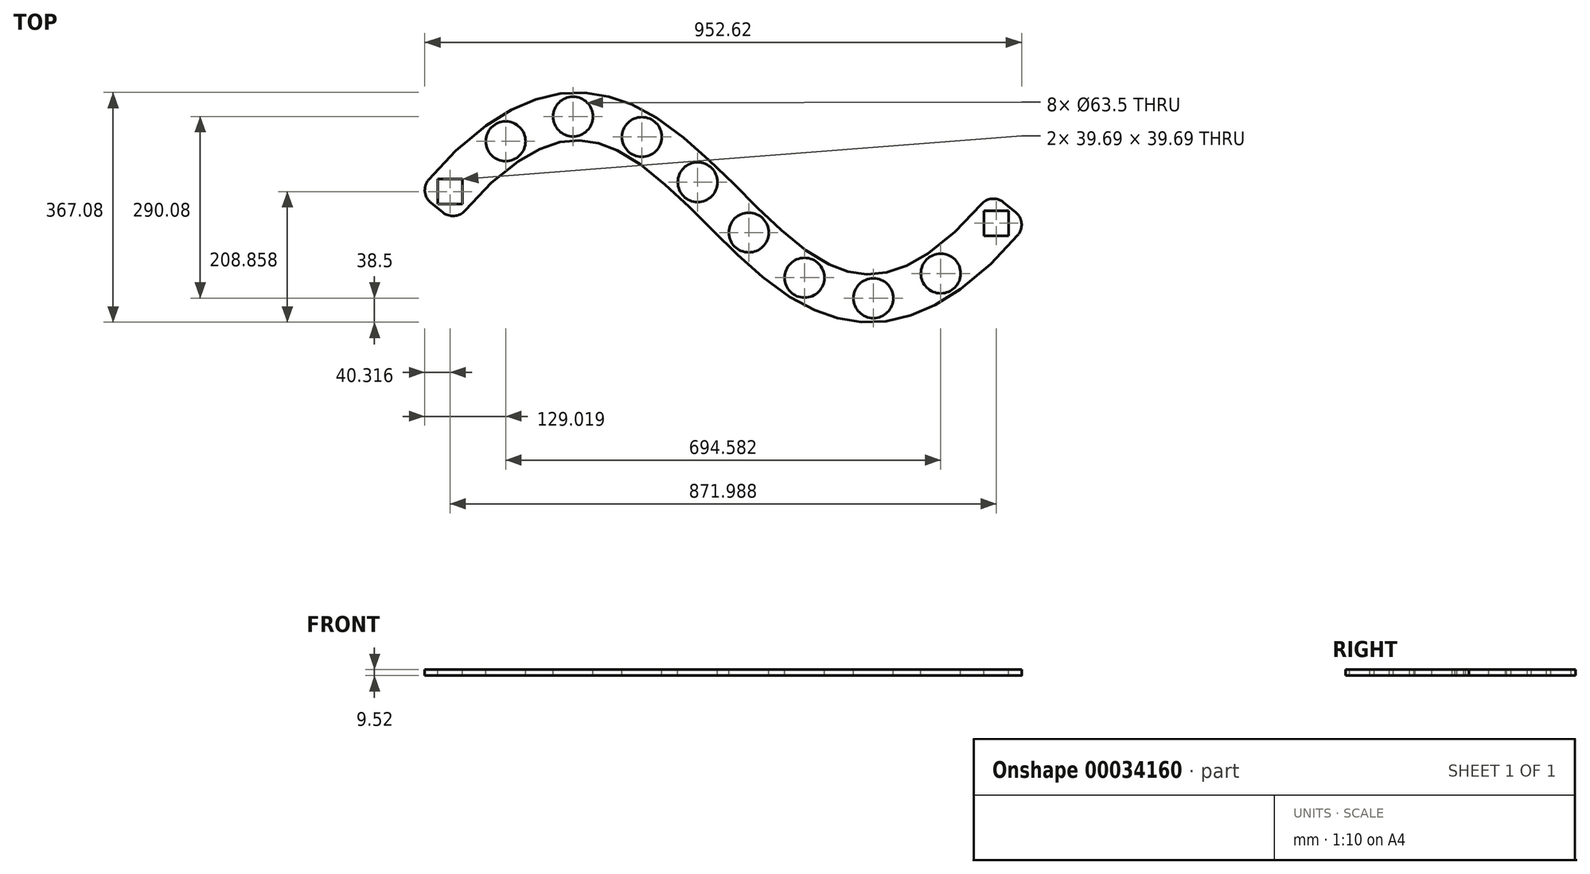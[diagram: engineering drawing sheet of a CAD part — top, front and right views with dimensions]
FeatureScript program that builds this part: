
annotation { "Feature Type Name" : "Feature", "Feature Type Description" : "" }
export const myFeature = defineFeature(function(context is Context, id is Id, definition is map)
    precondition{}
    {
        {
            var Q0;
            Q0=qCreatedBy(makeId("Top.planeOp"),FACE);
            var sketch = newSketch(context, id + "F0", { "sketchPlane" : qUnion([Q0])});
            skFitSpline(sketch, "E0", {"points": [v(457.2, 0) * mm, v(0, 0) * mm, v(-457.2, 0) * mm], "startDerivative": vector(-1234.52, -1508.68) * mm, "endDerivative": vector(-1234.52, -1508.68) * mm, "construction": true});
            skLineSegment(sketch, "E1", {"start": v(-251.45, 251.45) * mm, "end": v(251.45, -251.45) * mm, "construction": true});
            skFitSpline(sketch, "E2.0", {"points": [v(427.71, 24.13) * mm, v(415.4, 9.08) * mm, v(391.56, -17.97) * mm, v(358.18, -49.96) * mm, v(332.45, -69.99) * mm, v(313.15, -82.4) * mm, v(299.33, -90.03) * mm, v(286.14, -96.08) * mm, v(273.56, -100.69) * mm, v(261.55, -103.98) * mm, v(250.01, -106.09) * mm, v(238.86, -107.1) * mm, v(227.98, -107.12) * mm, v(217.27, -106.2) * mm, v(206.62, -104.35) * mm, v(195.97, -101.6) * mm, v(185.25, -97.95) * mm, v(174.44, -93.43) * mm, v(159.9, -86.24) * mm, v(141.47, -75.14) * mm, v(119.04, -58.8) * mm, v(96.37, -39.9) * mm, v(73.49, -18.95) * mm, v(50.39, 3.5) * mm, v(27, 26.88) * mm, v(3.24, 50.64) * mm, v(-21.04, 74.24) * mm, v(-46, 97.12) * mm, v(-71.89, 118.73) * mm, v(-98.95, 138.49) * mm, v(-122.74, 152.87) * mm, v(-142.68, 162.75) * mm, v(-158.11, 169.22) * mm, v(-174.04, 174.65) * mm, v(-190.48, 178.9) * mm, v(-207.39, 181.84) * mm, v(-224.73, 183.35) * mm, v(-242.44, 183.32) * mm, v(-260.43, 181.67) * mm, v(-278.62, 178.34) * mm, v(-296.95, 173.3) * mm, v(-315.36, 166.54) * mm, v(-333.84, 158.04) * mm, v(-352.38, 147.8) * mm, v(-377.21, 131.8) * mm, v(-408.54, 107.32) * mm, v(-446.94, 70.43) * mm, v(-473.28, 40.51) * mm, v(-486.69, 24.13) * mm]});
            skLineSegment(sketch, "E3", {"start": v(-486.69, 24.13) * mm, "end": v(-457.2, 0) * mm});
            skLineSegment(sketch, "E4", {"start": v(427.71, 24.13) * mm, "end": v(457.2, 0) * mm});
            skFitSpline(sketch, "E5.0", {"points": [v(486.69, -24.13) * mm, v(473.28, -40.51) * mm, v(446.94, -70.43) * mm, v(408.54, -107.32) * mm, v(377.21, -131.8) * mm, v(352.38, -147.8) * mm, v(333.84, -158.04) * mm, v(315.36, -166.54) * mm, v(296.95, -173.3) * mm, v(278.62, -178.34) * mm, v(260.43, -181.67) * mm, v(242.44, -183.32) * mm, v(224.73, -183.35) * mm, v(207.39, -181.84) * mm, v(190.48, -178.9) * mm, v(174.04, -174.65) * mm, v(158.11, -169.22) * mm, v(142.68, -162.75) * mm, v(122.74, -152.87) * mm, v(98.95, -138.49) * mm, v(71.89, -118.73) * mm, v(46, -97.12) * mm, v(21.04, -74.24) * mm, v(-3.24, -50.64) * mm, v(-27, -26.88) * mm, v(-50.39, -3.5) * mm, v(-73.49, 18.95) * mm, v(-96.37, 39.9) * mm, v(-119.04, 58.8) * mm, v(-141.47, 75.14) * mm, v(-159.9, 86.24) * mm, v(-174.44, 93.43) * mm, v(-185.25, 97.95) * mm, v(-195.97, 101.6) * mm, v(-206.62, 104.35) * mm, v(-217.27, 106.2) * mm, v(-227.98, 107.12) * mm, v(-238.86, 107.1) * mm, v(-250.01, 106.09) * mm, v(-261.55, 103.98) * mm, v(-273.56, 100.69) * mm, v(-286.14, 96.08) * mm, v(-299.33, 90.03) * mm, v(-313.15, 82.4) * mm, v(-332.45, 69.99) * mm, v(-358.18, 49.96) * mm, v(-391.56, 17.97) * mm, v(-415.4, -9.08) * mm, v(-427.71, -24.13) * mm]});
            skLineSegment(sketch, "E6", {"start": v(-457.2, 0) * mm, "end": v(-427.71, -24.13) * mm});
            skLineSegment(sketch, "E7", {"start": v(457.2, 0) * mm, "end": v(486.69, -24.13) * mm});
            skLineSegment(sketch, "E8", {"start": v(457.2, 0) * mm, "end": v(-457.2, 0) * mm, "construction": true});
            skSolve(sketch);
        }
        {
            var Q0;
            Q0=makeQuery(id+"F0.imprint","IMPRINT",FACE,{"disambiguationData":[TD([[makeQuery(id+"F0.imprint","IMPRINT",EDGE,{"derivedFrom":sQuery(id+"F0.wireOp",EDGE,"E0")}),-1.0]])]});
            var Q1;
            Q1=makeQuery(id+"F0.imprint","IMPRINT",FACE,{"disambiguationData":[TD([[makeQuery(id+"F0.imprint","IMPRINT",EDGE,{"derivedFrom":sQuery(id+"F0.wireOp",EDGE,"E2.0")}),1.0]])]});
            extrude(context, id + "F1", {"entities" : qUnion([Q0, Q1]), "endBound" : BoundingType.SYMMETRIC, "depth" : 9.52 * mm});
        }
        {
            var Q0;
            Q0=makeQuery(id+"F1.opExtrude","SWEPT_EDGE",EDGE,{"disambiguationData":[OSD([sQuery(id+"F0.wireOp",EDGE,"E5.0"),sQuery(id+"F0.wireOp",EDGE,"E6")])]});
            var Q1;
            Q1=makeQuery(id+"F1.opExtrude","SWEPT_EDGE",EDGE,{"disambiguationData":[OSD([sQuery(id+"F0.wireOp",EDGE,"E2.0"),sQuery(id+"F0.wireOp",EDGE,"E3")])]});
            var Q2;
            Q2=makeQuery(id+"F1.opExtrude","SWEPT_EDGE",EDGE,{"disambiguationData":[OSD([sQuery(id+"F0.wireOp",EDGE,"E5.0"),sQuery(id+"F0.wireOp",EDGE,"E7")])]});
            var Q3;
            Q3=makeQuery(id+"F1.opExtrude","SWEPT_EDGE",EDGE,{"disambiguationData":[OSD([sQuery(id+"F0.wireOp",EDGE,"E2.0"),sQuery(id+"F0.wireOp",EDGE,"E4")])]});
            fillet(context, id + "F2", {"entities" : qUnion([Q0, Q1, Q2, Q3]), "radius" : 25.4 * mm, "tangentPropagation" : true, "allowEdgeOverflow" : false});
        }
        {
            var Q0;
            Q0=makeQuery(id+"F1.opExtrude","CAP_FACE",FACE,{"disambiguationData":[OSD([sQuery(id+"F0.wireOp",EDGE,"E2.0"),sQuery(id+"F0.wireOp",EDGE,"E3"),sQuery(id+"F0.wireOp",EDGE,"E4"),sQuery(id+"F0.wireOp",EDGE,"E5.0"),sQuery(id+"F0.wireOp",EDGE,"E6"),sQuery(id+"F0.wireOp",EDGE,"E7")])],"isStart":false});
            var sketch = newSketch(context, id + "F3", { "sketchPlane" : qUnion([Q0])});
            skLineSegment(sketch, "E9.rect.bottom", {"start": v(-416.15, 45.16) * mm, "end": v(-455.84, 45.16) * mm});
            skLineSegment(sketch, "E9.rect.top", {"start": v(-416.15, 5.47) * mm, "end": v(-455.84, 5.47) * mm});
            skLineSegment(sketch, "E9.rect.left", {"start": v(-416.15, 45.16) * mm, "end": v(-416.15, 5.47) * mm});
            skLineSegment(sketch, "E9.rect.right", {"start": v(-455.84, 45.16) * mm, "end": v(-455.84, 5.47) * mm});
            skPoint(sketch, "E9.rect.middle", {"position": v(-436, 25.32) * mm});
            skLineSegment(sketch, "E10.rect.bottom", {"start": v(455.84, -5.47) * mm, "end": v(416.15, -5.47) * mm});
            skLineSegment(sketch, "E10.rect.top", {"start": v(455.84, -45.16) * mm, "end": v(416.15, -45.16) * mm});
            skLineSegment(sketch, "E10.rect.left", {"start": v(455.84, -5.47) * mm, "end": v(455.84, -45.16) * mm});
            skLineSegment(sketch, "E10.rect.right", {"start": v(416.15, -5.47) * mm, "end": v(416.15, -45.16) * mm});
            skPoint(sketch, "E10.rect.middle", {"position": v(436, -25.32) * mm});
            skPoint(sketch, "E11", {"position": v(475.96, -25.32) * mm});
            skLineSegment(sketch, "E12", {"start": v(-456.9, -0.24) * mm, "end": v(-436, 25.32) * mm});
            skLineSegment(sketch, "E13", {"start": v(436, -25.32) * mm, "end": v(456.9, 0.24) * mm});
            skPoint(sketch, "E14", {"position": v(-475.96, 25.32) * mm});
            skSolve(sketch);
        }
        {
            var Q0;
            Q0 = qSketchRegion(id + "F3", true);
            extrude(context, id + "F4", {"entities" : qUnion([Q0]), "operationType" : NewBodyOperationType.REMOVE, "endBound" : BoundingType.THROUGH_ALL, "oppositeDirection" : true, "depth" : 25.4 * mm});
        }
        {
            var Q0;
            Q0=makeQuery(id+"F1.opExtrude","CAP_FACE",FACE,{"disambiguationData":[OSD([sQuery(id+"F0.wireOp",EDGE,"E2.0"),sQuery(id+"F0.wireOp",EDGE,"E3"),sQuery(id+"F0.wireOp",EDGE,"E4"),sQuery(id+"F0.wireOp",EDGE,"E5.0"),sQuery(id+"F0.wireOp",EDGE,"E6"),sQuery(id+"F0.wireOp",EDGE,"E7")])],"isStart":false});
            var sketch = newSketch(context, id + "F5", { "sketchPlane" : qUnion([Q0])});
            skPoint(sketch, "E15", {"position": v(-347.3, 105.57) * mm});
            skPoint(sketch, "E16", {"position": v(-239.69, 145.04) * mm});
            skPoint(sketch, "E17", {"position": v(-40.8, 40.23) * mm});
            skPoint(sketch, "E18", {"position": v(40.8, -40.23) * mm});
            skPoint(sketch, "E19", {"position": v(129.8, -112.45) * mm});
            skPoint(sketch, "E20", {"position": v(347.3, -105.57) * mm});
            skPoint(sketch, "E21", {"position": v(239.69, -145.04) * mm});
            skPoint(sketch, "E22", {"position": v(-129.8, 112.45) * mm});
            skFitSpline(sketch, "E23.0", {"points": [v(457.2, 0) * mm, v(251.45, -251.45) * mm, v(0, 0) * mm, v(-251.45, 251.45) * mm, v(-457.2, 0) * mm], "construction": true});
            skLineSegment(sketch, "E24", {"start": v(-347.3, 105.57) * mm, "end": v(-239.69, 145.04) * mm, "construction": true});
            skLineSegment(sketch, "E25", {"start": v(-239.69, 145.04) * mm, "end": v(-129.8, 112.45) * mm, "construction": true});
            skLineSegment(sketch, "E26", {"start": v(-40.8, 40.23) * mm, "end": v(-129.8, 112.45) * mm, "construction": true});
            skLineSegment(sketch, "E27", {"start": v(129.8, -112.45) * mm, "end": v(40.8, -40.23) * mm, "construction": true});
            skLineSegment(sketch, "E28", {"start": v(239.69, -145.04) * mm, "end": v(129.8, -112.45) * mm, "construction": true});
            skLineSegment(sketch, "E29", {"start": v(347.3, -105.57) * mm, "end": v(239.69, -145.04) * mm, "construction": true});
            skLineSegment(sketch, "E30", {"start": v(347.3, -105.57) * mm, "end": v(457.2, 0) * mm, "construction": true});
            skLineSegment(sketch, "E31", {"start": v(-347.3, 105.57) * mm, "end": v(-457.2, 0) * mm, "construction": true});
            skLineSegment(sketch, "E32", {"start": v(-40.8, 40.23) * mm, "end": v(40.8, -40.23) * mm, "construction": true});
            skSolve(sketch);
        }
        {
            var Q0;
            Q0=sQuery(id+"F5.wireOp",VERTEX,"E15");
            var Q1;
            Q1=sQuery(id+"F5.wireOp",VERTEX,"E16");
            var Q2;
            Q2=sQuery(id+"F5.wireOp",VERTEX,"E22");
            var Q3;
            Q3=sQuery(id+"F5.wireOp",VERTEX,"E17");
            var Q4;
            Q4=sQuery(id+"F5.wireOp",VERTEX,"E18");
            var Q5;
            Q5=sQuery(id+"F5.wireOp",VERTEX,"E19");
            var Q6;
            Q6=sQuery(id+"F5.wireOp",VERTEX,"E21");
            var Q7;
            Q7=sQuery(id+"F5.wireOp",VERTEX,"E20");
            var Q8;
            Q8=makeQuery(id+"F1.opExtrude","SWEPT_BODY",BODY,{"disambiguationData":[OSD([sQuery(id+"F0.wireOp",EDGE,"E2.0"),sQuery(id+"F0.wireOp",EDGE,"E3"),sQuery(id+"F0.wireOp",EDGE,"E4"),sQuery(id+"F0.wireOp",EDGE,"E5.0"),sQuery(id+"F0.wireOp",EDGE,"E6"),sQuery(id+"F0.wireOp",EDGE,"E7")])]});
            hole(context, id + "F6", {"style" : HoleStyle.SIMPLE, "holeDiameter" : 63.5 * mm, "endStyle" : HoleEndStyle.THROUGH, "locations" : qUnion([Q0, Q1, Q2, Q3, Q4, Q5, Q6, Q7]), "scope" : qUnion([Q8])});
        }
    });
